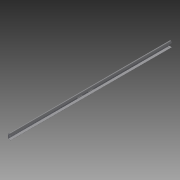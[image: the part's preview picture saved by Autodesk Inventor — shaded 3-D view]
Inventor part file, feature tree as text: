
AUTODESK INVENTOR PART (.ipt)
format: ipt  version: 2015 (Build 190159000, 159)  size: 294,912 bytes
history: native  units: in
note: dims shown in document units (in); Inventor stores cm internally (conversion verified against a paired STEP export)
features: sketch x9, projected_geometry x6, hole x5, extrude x4
ambient origin geometry x8: Origin, YZ Plane, XZ Plane, XY Plane, X Axis, Y Axis, Z Axis, Center Point
bodies: Solid1 (feature_tree)
feature tree (24):
  extrude  "Extrusion1"  Depth=2.125in
  hole  "Hole1"  [1 undecoded]
  extrude  "Extrusion2"  TaperAngle=90.0deg  [1 undecoded]
  hole  "Hole2"  [1 undecoded]
  extrude  "Extrusion3"  Depth=0.25in
  hole  "Hole5"  [1 undecoded]
  hole  "Hole6"  [1 undecoded]
  extrude  "Extrusion4"  TaperAngle=90.0deg  [1 undecoded]
  hole  "Hole7"  [1 undecoded]
  sketch  "Sketch1"  dims[d0=0.5in d1=2.125in]
  sketch  "Sketch2"  dims[d2=0.5in d3=180.0deg]
  projected_geometry  "Projected Loop1"
  sketch  "Sketch3"  dims[d4=2.125in d5=90.0deg]
  projected_geometry  "Projected Loop2"
  sketch  "Sketch4"  dims[d6=0.5in d7=0.5in]
  projected_geometry  "Projected Loop3"
  sketch  "Sketch6"  dims[d8=0.25in d9=0.25in]
  projected_geometry  "Projected Loop5"
  sketch  "Sketch8"  dims[d10=0.25in d11=150.0deg]
  projected_geometry  "Projected Loop7"
  sketch  "Sketch9"  dims[d12=0.25in d13=30.0deg]
  sketch  "Sketch10"  dims[d14=0.0625in d15=90.0deg]
  sketch  "Sketch11"  dims[d16=1.0625in d17=0.25in d18=60.0deg d19=120.0deg d20=90.0deg d21=0.0625in d22=0.25in d23=0.25in d24=0.0625in d25=0.3125in d26=0.0in d27=66.5in d28=0.0in d29=0.75in d30=1.5in d33=0.375in d34=0.75in d35=0.375in d36=0.25in d37=0.5635in d38=1.0in d39=0.8108in d45=0.5in d46=0.625in d47=1.25in d48=0.5in d49=0.625in d50=0.375in d51=0.75in d52=0.5in d53=0.5in d54=1.125in d55=1.125in d56=0.125in d57=0.125in d58=0.125in d59=0.125in d60=0.125in d61=0.125in d62=0.125in d63=0.125in d64=0.125in d65=0.125in d66=0.125in d67=0.125in d68=1.0in d69=0.0in d70=2.5in d71=3.0in d72=3.5in d73=4.0in d74=0.5in d77=0.5in d78=0.25in d79=0.75in d80=0.375in d81=0.25in d82=0.5635in d83=1.0in d84=0.8108in d98=2.0in d99=1.0in d100=2.0in d101=1.0in d102=31.0in d103=35.5in d104=0.25in d105=0.25in d106=1.0in d107=0.0in d120=1.0in d121=1.0in d122=0.75in d123=0.75in d124=7.5in d125=30.5in d126=0.25in d127=0.75in d128=0.375in d129=0.25in d130=0.5635in d131=1.0in d132=0.8108in d135=0.5in d136=0.5in d137=0.5in d138=1.0in d139=0.25in d140=0.75in d141=0.375in d142=0.25in d143=0.5635in d144=1.0in d145=0.8108in d146=0.75in d147=0.0in d148=0.7812in d149=2.75in d150=0.25in d151=0.75in d152=0.375in d153=0.25in d154=0.5635in d155=1.0in d156=0.8108in]
  projected_geometry  "Projected Loop8"
note: 7 required parameter values undecoded (feature->parameter linkage not recoverable at this tier; creation-order binding heuristic only, values carry confidence <= 0.55)
